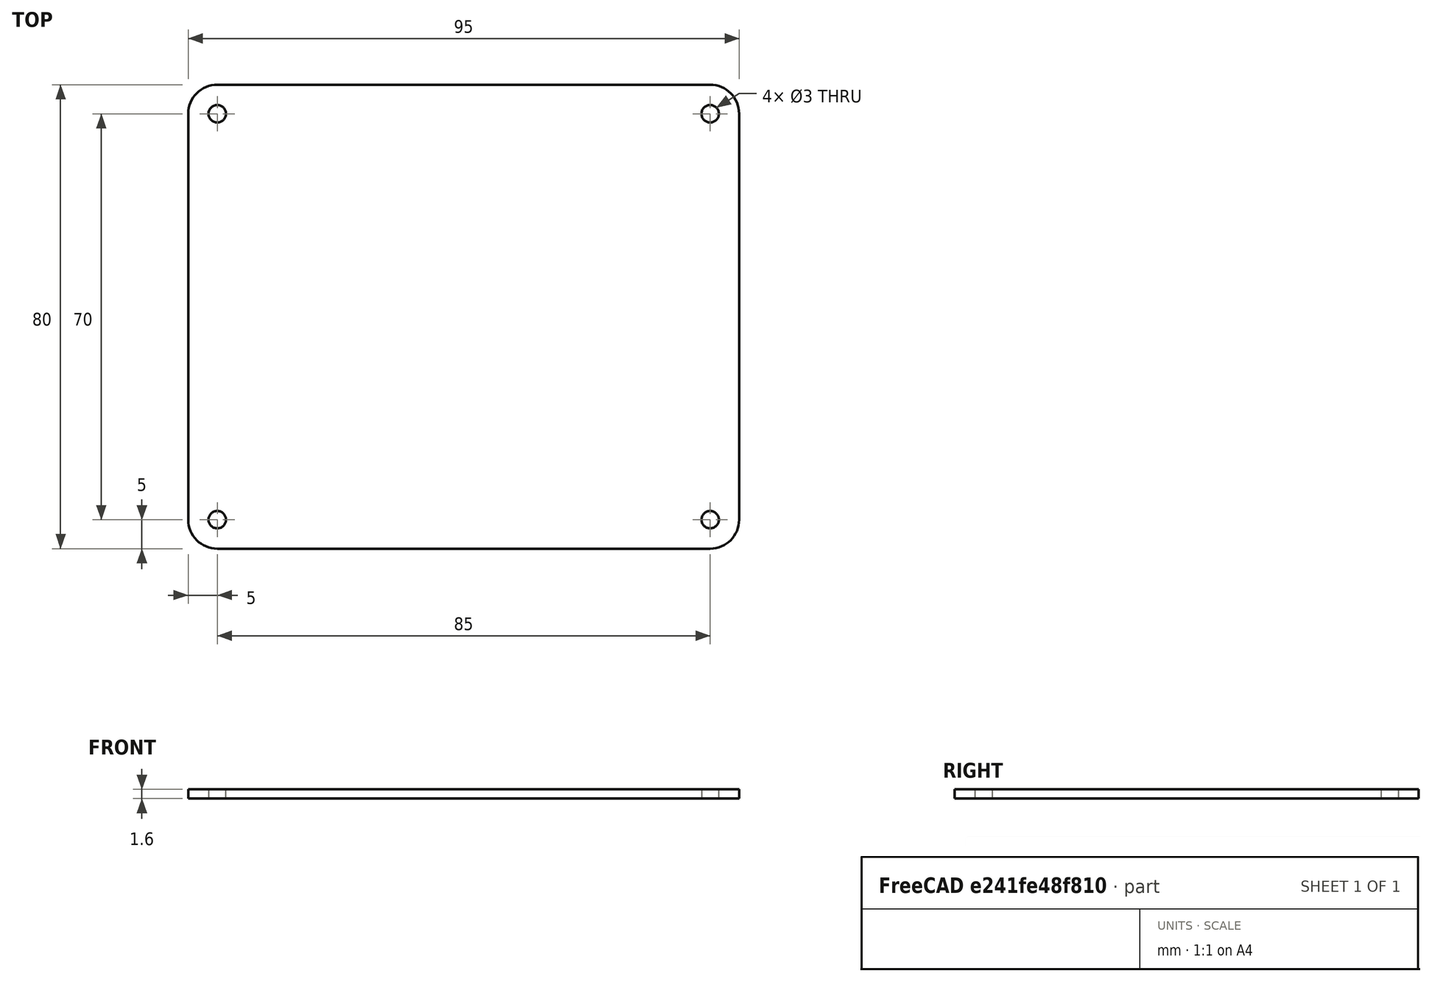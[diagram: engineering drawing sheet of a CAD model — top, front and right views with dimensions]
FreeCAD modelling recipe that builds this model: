
FCSTD DOCUMENT  (FreeCAD 0.20R29177 (Git))
Label: PCB
License: All rights reserved
LicenseURL: http://en.wikipedia.org/wiki/All_rights_reserved
objects: Sketcher::SketchObject×1, PartDesign::Pad×1, PartDesign::Body×1
note: 4 computed .brp shape members not serialized (recipe doc carries the construction recipe); baked Part::Feature solids carry a one-line shape summary decoded from their .brp

FEATURE [Sketcher::SketchObject] Sketch
  FullyConstrained = true
  MapMode = 5
  Support = -> [XY_Plane]
  sketch-geometry (14):
    g0: ArcOfCircle CenterX=-42.5 CenterY=35 CenterZ=0 NormalX=0 NormalY=0 NormalZ=1 AngleXU=0 Radius=5 StartAngle=1.5708 EndAngle=3.14159
    g1: LineSegment StartX=-42.5 StartY=40 StartZ=0 EndX=42.5 EndY=40 EndZ=0
    g2: ArcOfCircle CenterX=42.5 CenterY=35 CenterZ=0 NormalX=0 NormalY=0 NormalZ=1 AngleXU=0 Radius=5 StartAngle=1e-16 EndAngle=1.5708
    g3: LineSegment StartX=47.5 StartY=35 StartZ=0 EndX=47.5 EndY=-35 EndZ=0
    g4: ArcOfCircle CenterX=42.5 CenterY=-35 CenterZ=0 NormalX=0 NormalY=0 NormalZ=1 AngleXU=0 Radius=5 StartAngle=4.71239 EndAngle=6.28319
    g5: LineSegment StartX=42.5 StartY=-40 StartZ=0 EndX=-42.5 EndY=-40 EndZ=0
    g6: ArcOfCircle CenterX=-42.5 CenterY=-35 CenterZ=0 NormalX=0 NormalY=0 NormalZ=1 AngleXU=0 Radius=5 StartAngle=3.14159 EndAngle=4.71239
    g7: LineSegment StartX=-47.5 StartY=-35 StartZ=0 EndX=-47.5 EndY=35 EndZ=0
    g8: GeomPoint X=-47.5 Y=40 Z=0
    g9: GeomPoint X=47.5 Y=-40 Z=0
    g10: Circle CenterX=-42.5 CenterY=35 CenterZ=0 NormalX=0 NormalY=0 NormalZ=1 AngleXU=0 Radius=1.5
    g11: Circle CenterX=-42.5 CenterY=-35 CenterZ=0 NormalX=0 NormalY=0 NormalZ=1 AngleXU=0 Radius=1.5
    g12: Circle CenterX=42.5 CenterY=-35 CenterZ=0 NormalX=0 NormalY=0 NormalZ=1 AngleXU=0 Radius=1.5
    g13: Circle CenterX=42.5 CenterY=35 CenterZ=0 NormalX=0 NormalY=0 NormalZ=1 AngleXU=0 Radius=1.5
  constraints (31):
    c: Tangent(g0,g1) = 1.5708
    c: Tangent(g1,g2) = 1.5708
    c: Tangent(g2,g3) = 1.5708
    c: Tangent(g3,g4) = 1.5708
    c: Tangent(g4,g5) = 1.5708
    c: Tangent(g5,g6) = 1.5708
    c: Tangent(g6,g7) = 1.5708
    c: Tangent(g7,g0) = 1.5708
    c: Horizontal(g1)
    c: Horizontal(g5)
    c: Vertical(g3)
    c: Vertical(g7)
    c: Equal(g0,g2)
    c: Equal(g2,g4)
    c: Equal(g4,g6)
    c: PointOnObject(g8,g1)
    c: PointOnObject(g8,g7)
    c: PointOnObject(g9,g3)
    c: PointOnObject(g9,g5)
    c: DistanceX(g0,g2) = 95
    c: Symmetric(g8,g9,g-1)
    c: Radius(g0) = 5
    c: DistanceY(g5,g0) = 80
    c: Coincident(g10,g0)
    c: Coincident(g11,g6)
    c: Coincident(g12,g4)
    c: Coincident(g13,g2)
    c: Equal(g10,g13)
    c: Equal(g10,g12)
    c: Equal(g10,g11)
    c: Diameter(g10) = 3
FEATURE [PartDesign::Pad] Pad
  Direction = (0,0,1)
  Length = 1.6
  Length2 = 10
  Profile = -> Sketch
  ReferenceAxis = -> Sketch [N_Axis]
  Type = 0
FEATURE [PartDesign::Body] Body
  Group = -> [Sketch,Pad]
  Origin = -> Origin
  Tip = -> Pad
